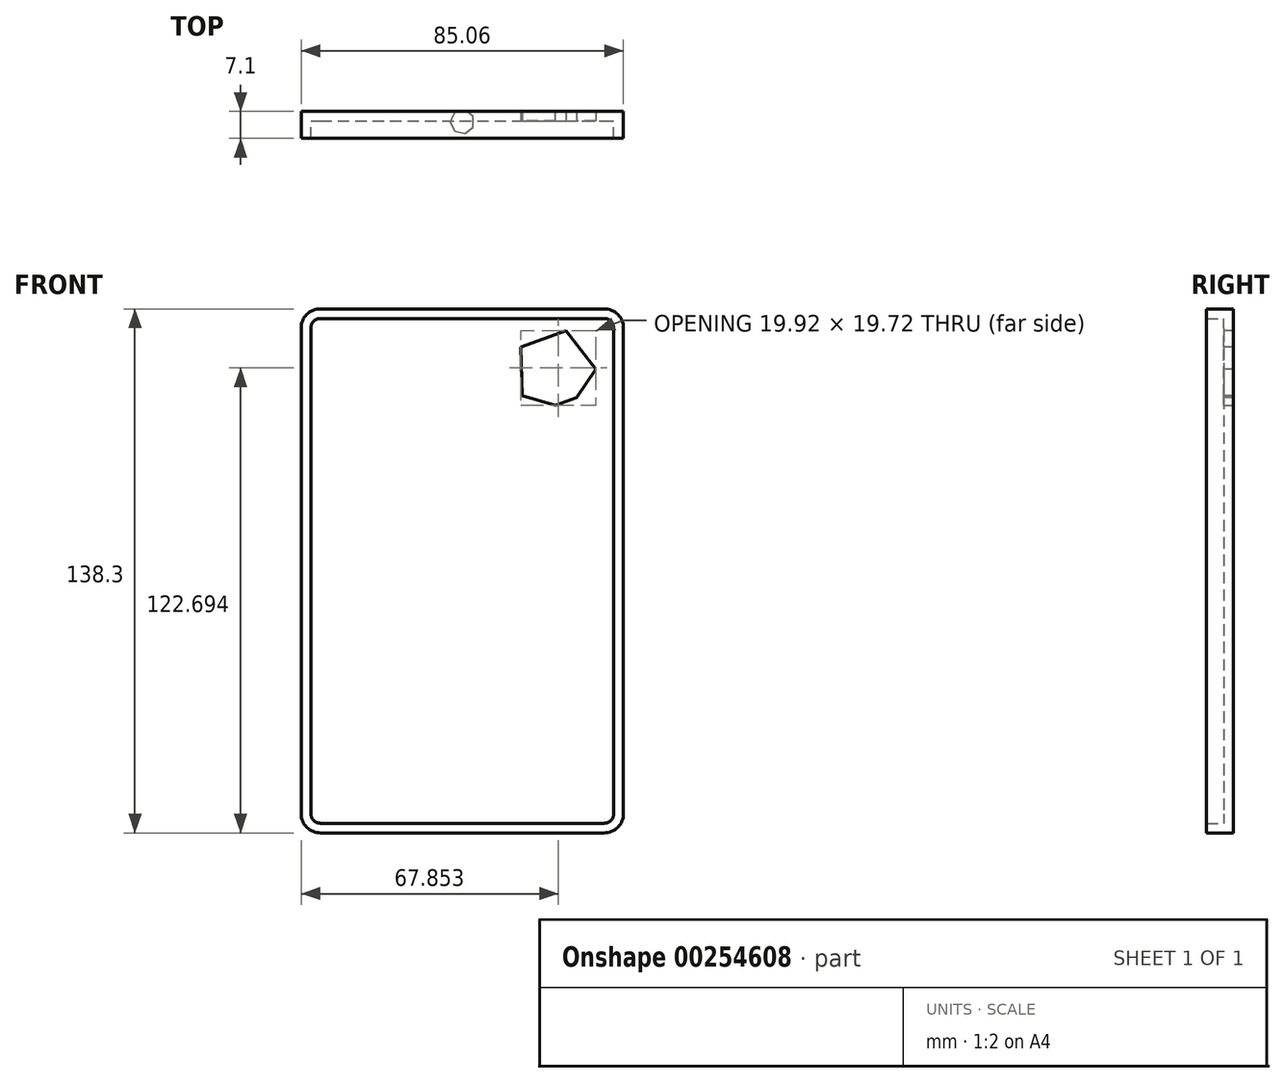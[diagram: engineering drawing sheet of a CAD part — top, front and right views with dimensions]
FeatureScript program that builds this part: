
annotation { "Feature Type Name" : "Feature", "Feature Type Description" : "" }
export const myFeature = defineFeature(function(context is Context, id is Id, definition is map)
    precondition{}
    {
        {
            var Q0;
            Q0=qCreatedBy(makeId("Front.planeOp"),FACE);
            var sketch = newSketch(context, id + "F0", { "sketchPlane" : qUnion([Q0])});
            skLineSegment(sketch, "E0.left", {"start": v(0, 0) * mm, "end": v(0, 0) * mm});
            skLineSegment(sketch, "E1.bottom", {"start": v(-42.53, 69.15) * mm, "end": v(42.53, 69.15) * mm});
            skLineSegment(sketch, "E1.top", {"start": v(-42.53, -69.15) * mm, "end": v(42.53, -69.15) * mm});
            skLineSegment(sketch, "E1.left", {"start": v(-42.53, 69.15) * mm, "end": v(-42.53, -69.15) * mm});
            skLineSegment(sketch, "E1.right", {"start": v(42.53, 69.15) * mm, "end": v(42.53, -69.15) * mm});
            skPoint(sketch, "E1.middle", {"position": v(0, 0) * mm});
            skSolve(sketch);
        }
        {
            var Q0;
            Q0=makeQuery(id+"F0.imprint","IMPRINT",FACE,{"disambiguationData":[TD([[makeQuery(id+"F0.imprint","IMPRINT",EDGE,{"derivedFrom":sQuery(id+"F0.wireOp",EDGE,"E1.bottom")}),-1.0]])]});
            extrude(context, id + "F1", {"entities" : qUnion([Q0]), "depth" : 7.1 * mm});
        }
        {
            var Q0;
            Q0=makeQuery(id+"F1.opExtrude","SWEPT_EDGE",EDGE,{"disambiguationData":[OSD([sQuery(id+"F0.wireOp",EDGE,"E1.top"),sQuery(id+"F0.wireOp",EDGE,"E1.right")])]});
            var Q1;
            Q1=makeQuery(id+"F1.opExtrude","SWEPT_EDGE",EDGE,{"disambiguationData":[OSD([sQuery(id+"F0.wireOp",EDGE,"E1.top"),sQuery(id+"F0.wireOp",EDGE,"E1.left")])]});
            var Q2;
            Q2=makeQuery(id+"F1.opExtrude","SWEPT_EDGE",EDGE,{"disambiguationData":[OSD([sQuery(id+"F0.wireOp",EDGE,"E1.bottom"),sQuery(id+"F0.wireOp",EDGE,"E1.right")])]});
            var Q3;
            Q3=makeQuery(id+"F1.opExtrude","SWEPT_EDGE",EDGE,{"disambiguationData":[OSD([sQuery(id+"F0.wireOp",EDGE,"E1.bottom"),sQuery(id+"F0.wireOp",EDGE,"E1.left")])]});
            fillet(context, id + "F2", {"entities" : qUnion([Q0, Q1, Q2, Q3]), "radius" : 5.08 * mm, "tangentPropagation" : true, "allowEdgeOverflow" : false});
        }
        {
            var Q0;
            Q0=makeQuery(id+"F1.opExtrude","CAP_FACE",FACE,{"disambiguationData":[OSD([sQuery(id+"F0.wireOp",EDGE,"E1.bottom"),sQuery(id+"F0.wireOp",EDGE,"E1.top"),sQuery(id+"F0.wireOp",EDGE,"E1.left"),sQuery(id+"F0.wireOp",EDGE,"E1.right")])],"isStart":false});
            shell(context, id + "F3", {"entities" : qUnion([Q0]), "thickness" : 2.54 * mm});
        }
        {
            var Q0;
            Q0=makeQuery(id+"F3.opShell","OFFSET_FACE",FACE,{"disambiguationData":[OSD([sQuery(id+"F0.wireOp",EDGE,"E1.bottom"),sQuery(id+"F0.wireOp",EDGE,"E1.top"),sQuery(id+"F0.wireOp",EDGE,"E1.left"),sQuery(id+"F0.wireOp",EDGE,"E1.right")])]});
            var sketch = newSketch(context, id + "F4", { "sketchPlane" : qUnion([Q0])});
            skCircle(sketch, "E2.cCircle", {"center": v(24.39, 52.93) * mm, "radius": 10.9 * mm, "construction": true});
            skLineSegment(sketch, "E2.0", {"start": v(28.09, 42.67) * mm, "end": v(15.78, 46.24) * mm});
            skLineSegment(sketch, "E2.1", {"start": v(15.78, 46.24) * mm, "end": v(15.36, 59.05) * mm});
            skLineSegment(sketch, "E2.2", {"start": v(15.36, 59.05) * mm, "end": v(27.42, 63.4) * mm});
            skLineSegment(sketch, "E2.3", {"start": v(27.42, 63.4) * mm, "end": v(35.28, 53.28) * mm});
            skLineSegment(sketch, "E2.4", {"start": v(35.28, 53.28) * mm, "end": v(28.09, 42.67) * mm});
            skSolve(sketch);
        }
        {
            var Q0;
            Q0=makeQuery(id+"F4.imprint","IMPRINT",FACE,{"disambiguationData":[TD([[makeQuery(id+"F4.imprint","IMPRINT",EDGE,{"derivedFrom":sQuery(id+"F4.wireOp",EDGE,"E2.0")}),-1.0]])]});
            extrude(context, id + "F5", {"entities" : qUnion([Q0]), "operationType" : NewBodyOperationType.REMOVE, "oppositeDirection" : true, "depth" : 25 * mm});
        }
        {
            var Q0;
            Q0=makeQuery(id+"F5.boolean.opBoolean","COPY",EDGE,{"derivedFrom":makeQuery(id+"F5.opExtrude","SWEPT_EDGE",EDGE,{"disambiguationData":[OSD([sQuery(id+"F4.wireOp",EDGE,"E2.0"),sQuery(id+"F4.wireOp",EDGE,"E2.4")])]})});
            var Q1;
            Q1=makeQuery(id+"F5.boolean.opBoolean","COPY",EDGE,{"derivedFrom":makeQuery(id+"F5.opExtrude","CAP_EDGE",EDGE,{"disambiguationData":[OSD([sQuery(id+"F4.wireOp",EDGE,"E2.0")])],"isStart":true})});
            var Q2;
            Q2=makeQuery(id+"F5.boolean.opBoolean","COPY",EDGE,{"derivedFrom":makeQuery(id+"F5.opExtrude","CAP_EDGE",EDGE,{"disambiguationData":[OSD([sQuery(id+"F4.wireOp",EDGE,"E2.4")])],"isStart":true})});
            var Q3;
            Q3=makeQuery(id+"F5.boolean.opBoolean","COPY",EDGE,{"derivedFrom":makeQuery(id+"F5.opExtrude","CAP_EDGE",EDGE,{"disambiguationData":[OSD([sQuery(id+"F4.wireOp",EDGE,"E2.3")])],"isStart":true})});
            var Q4;
            Q4=makeQuery(id+"F5.boolean.opBoolean","COPY",EDGE,{"derivedFrom":makeQuery(id+"F5.opExtrude","CAP_EDGE",EDGE,{"disambiguationData":[OSD([sQuery(id+"F4.wireOp",EDGE,"E2.2")])],"isStart":true})});
            var Q5;
            Q5=makeQuery(id+"F5.boolean.opBoolean","COPY",EDGE,{"derivedFrom":makeQuery(id+"F5.opExtrude","CAP_EDGE",EDGE,{"disambiguationData":[OSD([sQuery(id+"F4.wireOp",EDGE,"E2.1")])],"isStart":true})});
            chamfer(context, id + "F6", {"entities" : qUnion([Q0, Q1, Q2, Q3, Q4, Q5]), "width" : 5 * mm, "tangentPropagation" : true});
        }
        {
            var Q0;
            Q0=makeQuery(id+"F1.opExtrude","SWEPT_FACE",FACE,{"disambiguationData":[OSD([sQuery(id+"F0.wireOp",EDGE,"E1.top")])]});
            var sketch = newSketch(context, id + "F7", { "sketchPlane" : qUnion([Q0])});
            skCircle(sketch, "E3.cCircle", {"center": v(0, 2.73) * mm, "radius": 2.87 * mm, "construction": true});
            skLineSegment(sketch, "E3.0", {"start": v(2.87, 4.1) * mm, "end": v(2.87, 1.34) * mm});
            skLineSegment(sketch, "E3.1", {"start": v(2.87, 1.34) * mm, "end": v(0.7, -0.38) * mm});
            skLineSegment(sketch, "E3.2", {"start": v(0.7, -0.38) * mm, "end": v(-1.99, 0.24) * mm});
            skLineSegment(sketch, "E3.3", {"start": v(-1.99, 0.24) * mm, "end": v(-3.18, 2.73) * mm});
            skLineSegment(sketch, "E3.4", {"start": v(-3.18, 2.73) * mm, "end": v(-1.99, 5.21) * mm});
            skLineSegment(sketch, "E3.5", {"start": v(-1.99, 5.21) * mm, "end": v(0.7, 5.83) * mm});
            skLineSegment(sketch, "E3.6", {"start": v(0.7, 5.83) * mm, "end": v(2.87, 4.1) * mm});
            skPoint(sketch, "E3.0.midPoint", {"position": v(2.87, 2.73) * mm});
            skSolve(sketch);
        }
        {
            var Q0;
            Q0 = qSketchRegion(id + "F7", true);
            extrude(context, id + "F8", {"entities" : qUnion([Q0]), "operationType" : NewBodyOperationType.REMOVE, "oppositeDirection" : true, "depth" : 0.1 * mm});
        }
    });
